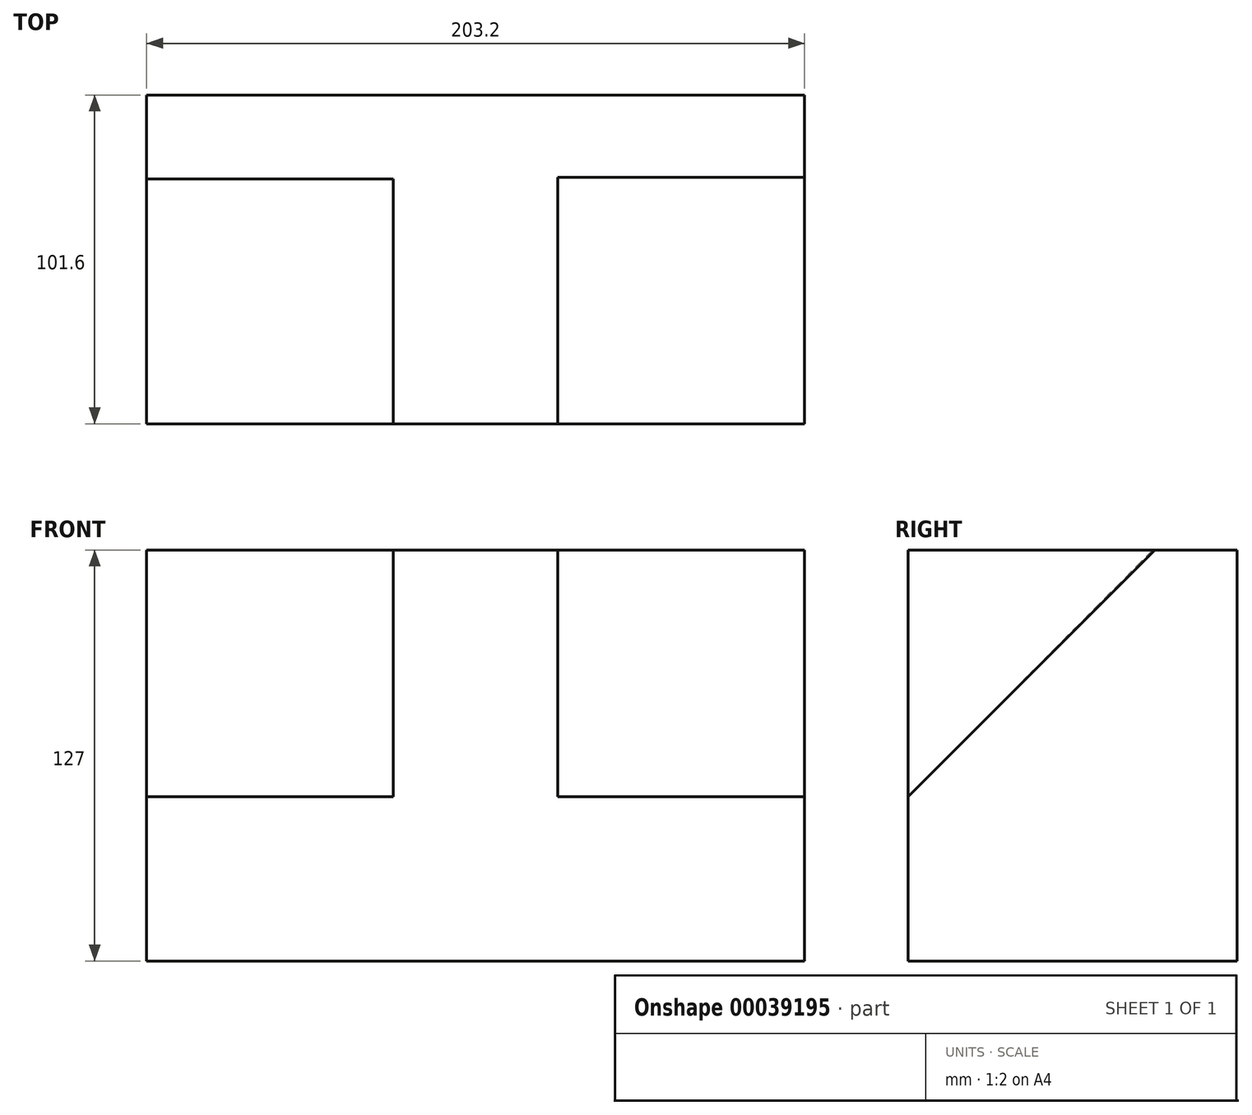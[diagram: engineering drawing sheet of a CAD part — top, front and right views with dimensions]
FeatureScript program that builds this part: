
annotation { "Feature Type Name" : "Feature", "Feature Type Description" : "" }
export const myFeature = defineFeature(function(context is Context, id is Id, definition is map)
    precondition{}
    {
        {
            var Q0;
            Q0=qCreatedBy(makeId("Top.planeOp"),FACE);
            var sketch = newSketch(context, id + "F4", { "sketchPlane" : qUnion([Q0])});
            skLineSegment(sketch, "E0.bottom", {"start": v(-56.11, 53.87) * mm, "end": v(147.09, 53.87) * mm});
            skLineSegment(sketch, "E0.top", {"start": v(-56.11, -47.73) * mm, "end": v(147.09, -47.73) * mm});
            skLineSegment(sketch, "E0.left", {"start": v(-56.11, 53.87) * mm, "end": v(-56.11, -47.73) * mm});
            skLineSegment(sketch, "E0.right", {"start": v(147.09, 53.87) * mm, "end": v(147.09, -47.73) * mm});
            skSolve(sketch);
        }
        {
            var Q0;
            Q0=qSketchRegion(id+"F4",true);
            var Q1;
            Q1=makeQuery(id+"F4.imprint","IMPRINT",FACE,{"disambiguationData":[TD([[makeQuery(id+"F4.imprint","IMPRINT",EDGE,{"derivedFrom":sQuery(id+"F4.wireOp",EDGE,"E0.bottom")}),-1.0]])]});
            extrude(context, id + "F5", {"entities" : qUnion([Q0, Q1]), "depth" : 127 * mm});
        }
        {
            var Q0;
            Q0=makeQuery(id+"F5.opExtrude","SWEPT_FACE",FACE,{"disambiguationData":[OSD([sQuery(id+"F4.wireOp",EDGE,"E0.right")])]});
            var sketch = newSketch(context, id + "F0", { "sketchPlane" : qUnion([Q0])});
            skLineSegment(sketch, "E1", {"start": v(53.87, 127) * mm, "end": v(28.47, 127) * mm});
            skLineSegment(sketch, "E2", {"start": v(-47.73, 0) * mm, "end": v(-47.73, 50.8) * mm});
            skLineSegment(sketch, "E3", {"start": v(-47.73, 50.8) * mm, "end": v(28.47, 127) * mm});
            skSolve(sketch);
        }
        {
            var Q0;
            Q0=qSketchRegion(id+"F0",true);
            var Q1;
            {var subQ2=sQuery(id+"F0.wireOp",EDGE,"E3");Q1=makeQuery(id+"F0.imprint","IMPRINT",FACE,{"disambiguationData":[TD([[makeQuery(id+"F0.imprint","IMPRINT",EDGE,{"derivedFrom":subQ2}),1.0]])]});}
            extrude(context, id + "F1", {"entities" : qUnion([Q0, Q1]), "operationType" : NewBodyOperationType.REMOVE, "oppositeDirection" : true, "depth" : 76.2 * mm});
        }
        {
            var Q0;
            Q0=makeQuery(id+"F5.opExtrude","SWEPT_FACE",FACE,{"disambiguationData":[OSD([sQuery(id+"F4.wireOp",EDGE,"E0.left")])]});
            var sketch = newSketch(context, id + "F2", { "sketchPlane" : qUnion([Q0])});
            skLineSegment(sketch, "E4", {"start": v(-53.25, 127.34) * mm, "end": v(-27.85, 127.36) * mm});
            skLineSegment(sketch, "E5", {"start": v(47.73, 0) * mm, "end": v(47.73, 50.8) * mm});
            skLineSegment(sketch, "E6", {"start": v(-27.85, 127) * mm, "end": v(47.73, 50.8) * mm});
            skSolve(sketch);
        }
        {
            var Q0;
            {var subQ2=sQuery(id+"F2.wireOp",EDGE,"E6");Q0=makeQuery(id+"F2.imprint","IMPRINT",FACE,{"disambiguationData":[TD([[makeQuery(id+"F2.imprint","IMPRINT",EDGE,{"derivedFrom":subQ2}),1.0]])]});}
            extrude(context, id + "F3", {"entities" : qUnion([Q0]), "operationType" : NewBodyOperationType.REMOVE, "oppositeDirection" : true, "depth" : 76.2 * mm});
        }
    });
